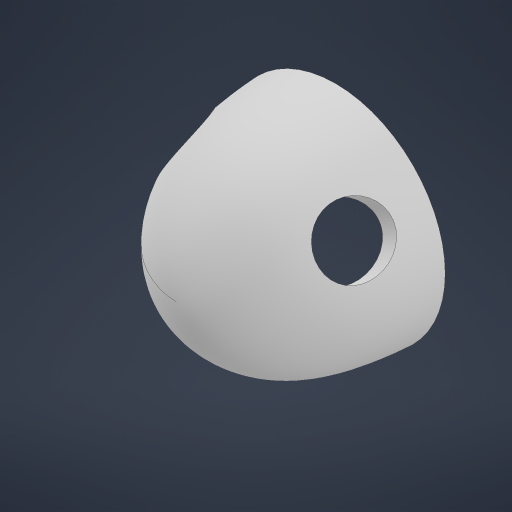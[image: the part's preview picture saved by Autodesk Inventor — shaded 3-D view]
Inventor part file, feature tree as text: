
AUTODESK INVENTOR PART (.ipt)
format: ipt  version: 2023.2 (Build 272271000, 271)  size: 413,184 bytes
history: native  units: mm
features: sketch x2, extrude x2, pattern_circular x2, revolve x1, plane x1
ambient origin geometry x8: Origin, YZ Plane, XZ Plane, XY Plane, X Axis, Y Axis, Z Axis, Center Point
bodies: Volumenkörper1 (feature_tree)
feature tree (8):
  revolve  "Umdrehung1"
  sketch  "Skizze2"  dims[d9=13.5mm d10=13.0mm d11=34.8mm d12=1.0mm d13=2.0mm d14=2.0mm d15=1.0mm d16=3.0mm d17=70.0mm d22=53.559595mm d23=62.806956mm d24=36.206962mm d25=34.985589mm d26=7.427193mm d27=25.251237mm d28=28.821993mm d29=29.003796mm d30=10.0mm d32=90.0deg d34=25.0mm d37=32.040499mm d38=24.953821mm d39=3.0mm d40=2.0mm d45=6.5mm d48=2.0mm d49=5.0mm d50=10.0mm d51=0.0mm d52=30.0mm d53=360.0deg d55=40.0mm d56=-32.0mm d57=10.0mm d58=0.0mm d59=30.0mm d60=360.0deg]
  extrude  "Extrusion1"  Depth=69.0mm
  pattern_circular  "Runde Anordnung1"  Count=16  [1 undecoded]
  plane  "Arbeitsebene1"
  extrude  "Extrusion2"  Depth=10.0mm
  pattern_circular  "Runde Anordnung2"  [2 undecoded]
  sketch  "Skizze1"  dims[d0=100.0mm d2=69.0mm d7=160.0mm]
note: 3 required parameter values undecoded (feature->parameter linkage not recoverable at this tier; creation-order binding heuristic only, values carry confidence <= 0.55)
